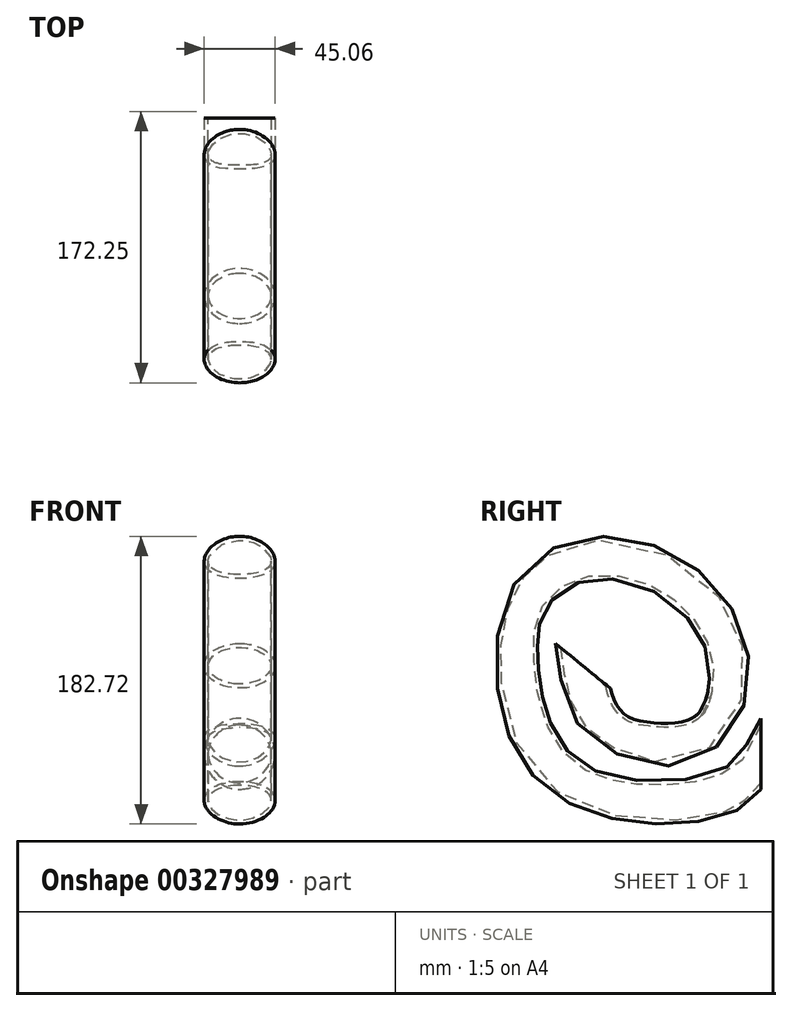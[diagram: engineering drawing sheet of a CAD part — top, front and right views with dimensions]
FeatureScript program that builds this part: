
annotation { "Feature Type Name" : "Feature", "Feature Type Description" : "" }
export const myFeature = defineFeature(function(context is Context, id is Id, definition is map)
    precondition{}
    {
        {
            var Q0;
            Q0=qCreatedBy(makeId("Front.planeOp"),FACE);
            var sketch = newSketch(context, id + "F0", { "sketchPlane" : qUnion([Q0])});
            skCircle(sketch, "E0", {"center": v(0, 0) * mm, "radius": 22.53 * mm});
            skSolve(sketch);
        }
        {
            var Q0;
            Q0=qCreatedBy(makeId("Right.planeOp"),FACE);
            var sketch = newSketch(context, id + "F1", { "sketchPlane" : qUnion([Q0])});
            skFitSpline(sketch, "E1", {"points": [v(0, 0) * mm, v(-20.52, -20.31) * mm, v(-65.92, -29.68) * mm, v(-118.51, -15.85) * mm, v(-149.08, 27.14) * mm, v(-144.13, 98.08) * mm, v(-97.38, 122.34) * mm, v(-41.2, 96.68) * mm, v(-23.67, 45.77) * mm, v(-50.19, 10.73) * mm, v(-97.38, 22.55) * mm, v(-113.12, 55.86) * mm], "startDerivative": vector(-247.98, -325.35) * mm, "endDerivative": vector(-111.84, 464.29) * mm});
            skSolve(sketch);
        }
        {
            var Q0;
            Q0=makeQuery(id+"F0.imprint","IMPRINT",FACE,{"disambiguationData":[TD([[makeQuery(id+"F0.imprint","IMPRINT",EDGE,{"derivedFrom":sQuery(id+"F0.wireOp",EDGE,"E0")}),1.0]])]});
            var Q1;
            Q1=sQuery(id+"F1.wireOp",EDGE,"E1");
            sweep(context, id + "F2", {"profiles" : qUnion([Q0]), "path" : qUnion([Q1])});
        }
        {
            var Q0;
            Q0=makeQuery(id+"F2.opSweep","CAP_FACE",FACE,{"disambiguationData":[OSD([sQuery(id+"F0.wireOp",EDGE,"E0"),sQuery(id+"F1.wireOp",VERTEX,"E1.end")])],"isStart":false});
            var Q1;
            Q1=makeQuery(id+"F2.opSweep","CAP_FACE",FACE,{"disambiguationData":[OSD([sQuery(id+"F0.wireOp",EDGE,"E0"),sQuery(id+"F1.wireOp",VERTEX,"E1.start")])],"isStart":true});
            shell(context, id + "F3", {"entities" : qUnion([Q0, Q1]), "thickness" : 2.5 * mm});
        }
    });
